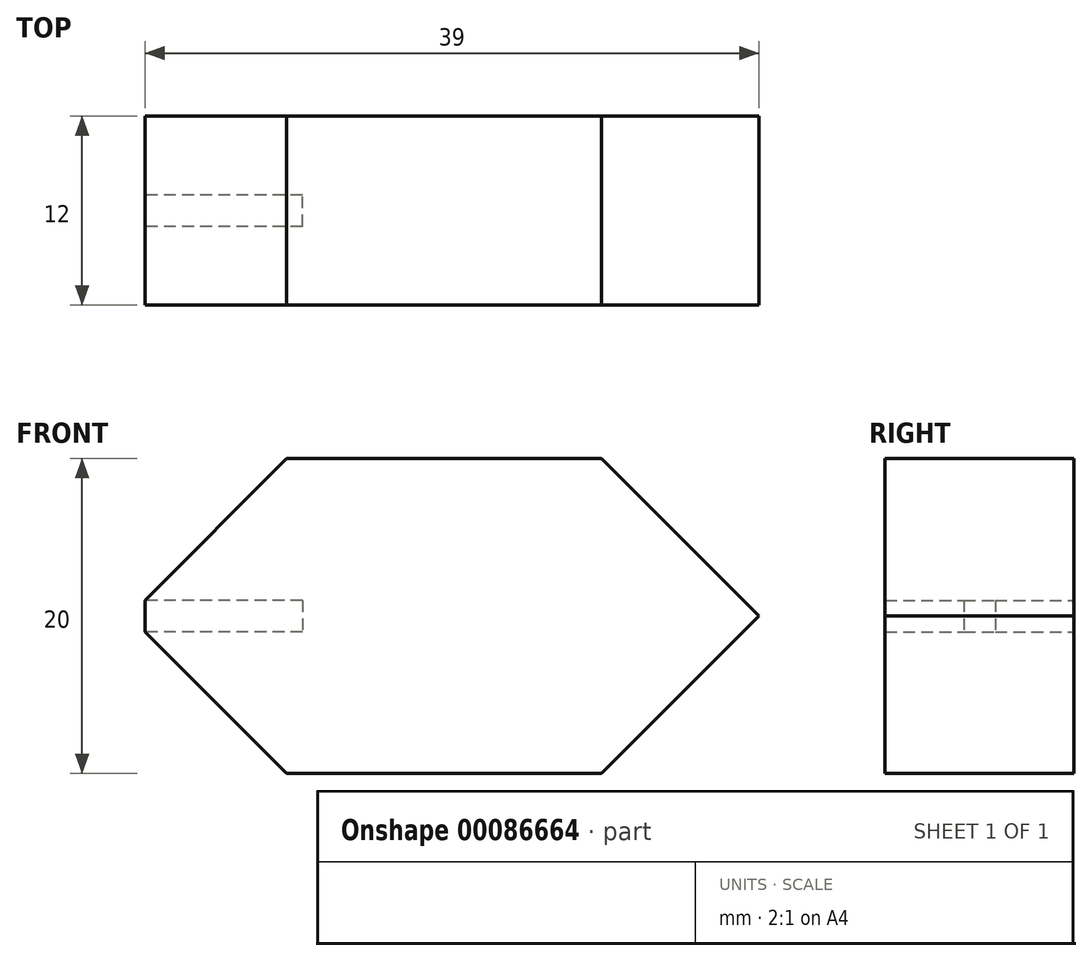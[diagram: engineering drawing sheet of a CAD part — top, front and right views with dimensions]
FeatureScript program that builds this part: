
annotation { "Feature Type Name" : "Feature", "Feature Type Description" : "" }
export const myFeature = defineFeature(function(context is Context, id is Id, definition is map)
    precondition{}
    {
        {
            var Q0;
            Q0=qCreatedBy(makeId("Front.planeOp"),FACE);
            var sketch = newSketch(context, id + "F0", { "sketchPlane" : qUnion([Q0])});
            skLineSegment(sketch, "E0", {"start": v(-9, 1) * mm, "end": v(0, 10) * mm});
            skLineSegment(sketch, "E1", {"start": v(0, 10) * mm, "end": v(20, 10) * mm});
            skLineSegment(sketch, "E2", {"start": v(20, 10) * mm, "end": v(30, 0) * mm});
            skLineSegment(sketch, "E3", {"start": v(30, 0) * mm, "end": v(20, -10) * mm});
            skLineSegment(sketch, "E4", {"start": v(20, -10) * mm, "end": v(0, -10) * mm});
            skLineSegment(sketch, "E5", {"start": v(0, -10) * mm, "end": v(-9, -1) * mm});
            skLineSegment(sketch, "E6", {"start": v(-9, -1) * mm, "end": v(-9, 1) * mm});
            skSolve(sketch);
        }
        {
            var Q0;
            Q0 = qSketchRegion(id + "F0", true);
            extrude(context, id + "F2", {"entities" : qUnion([Q0]), "depth" : 6 * mm, "hasSecondDirection" : true, "secondDirectionOppositeDirection" : true, "secondDirectionDepth" : 6 * mm});
        }
        {
            var Q0;
            Q0=makeQuery(id+"F2.opExtrude","SWEPT_FACE",FACE,{"disambiguationData":[OSD([sQuery(id+"F0.wireOp",EDGE,"E6")])]});
            var sketch = newSketch(context, id + "F1", { "sketchPlane" : qUnion([Q0])});
            skLineSegment(sketch, "E7.bottom", {"start": v(1, 1) * mm, "end": v(-1, 1) * mm});
            skLineSegment(sketch, "E7.top", {"start": v(1, -1) * mm, "end": v(-1, -1) * mm});
            skLineSegment(sketch, "E7.left", {"start": v(1, 1) * mm, "end": v(1, -1) * mm});
            skLineSegment(sketch, "E7.right", {"start": v(-1, 1) * mm, "end": v(-1, -1) * mm});
            skPoint(sketch, "E7.middle", {"position": v(0, 0) * mm});
            skSolve(sketch);
        }
        {
            var Q0;
            Q0 = qSketchRegion(id + "F1", true);
            extrude(context, id + "F3", {"entities" : qUnion([Q0]), "operationType" : NewBodyOperationType.REMOVE, "oppositeDirection" : true, "depth" : 10 * mm});
        }
    });
